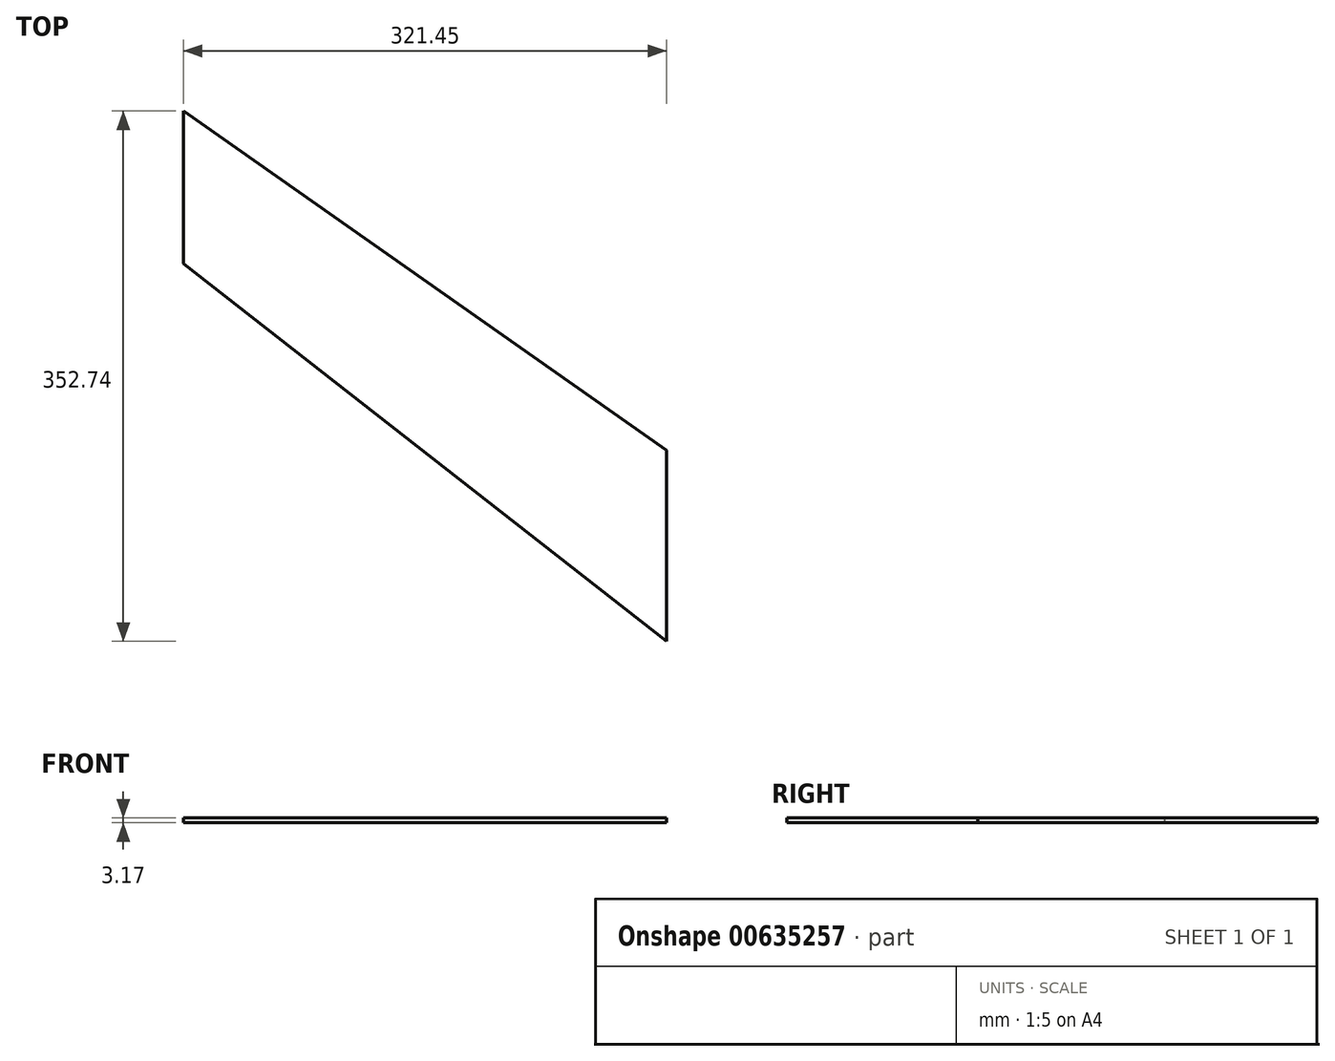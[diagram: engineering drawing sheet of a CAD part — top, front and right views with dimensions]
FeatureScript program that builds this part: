
annotation { "Feature Type Name" : "Feature", "Feature Type Description" : "" }
export const myFeature = defineFeature(function(context is Context, id is Id, definition is map)
    precondition{}
    {
        {
            var Q0;
            Q0=qCreatedBy(makeId("Top.planeOp"),FACE);
            var sketch = newSketch(context, id + "F0", { "sketchPlane" : qUnion([Q0])});
            skLineSegment(sketch, "E0", {"start": v(0, 0) * mm, "end": v(0, 127) * mm});
            skLineSegment(sketch, "E1", {"start": v(0, 127) * mm, "end": v(-321.45, 352.74) * mm});
            skLineSegment(sketch, "E2", {"start": v(-321.45, 352.74) * mm, "end": v(-321.45, 251.14) * mm});
            skLineSegment(sketch, "E3", {"start": v(-321.45, 251.14) * mm, "end": v(0, 0) * mm});
            skSolve(sketch);
        }
        {
            var Q0;
            Q0=makeQuery(id+"F0.imprint","IMPRINT",FACE,{"disambiguationData":[TD([[makeQuery(id+"F0.imprint","IMPRINT",EDGE,{"derivedFrom":sQuery(id+"F0.wireOp",EDGE,"E0")}),1.0]])]});
            extrude(context, id + "F1", {"entities" : qUnion([Q0]), "depth" : 3.17 * mm, "offsetDistance" : 25.4 * mm});
        }
    });
